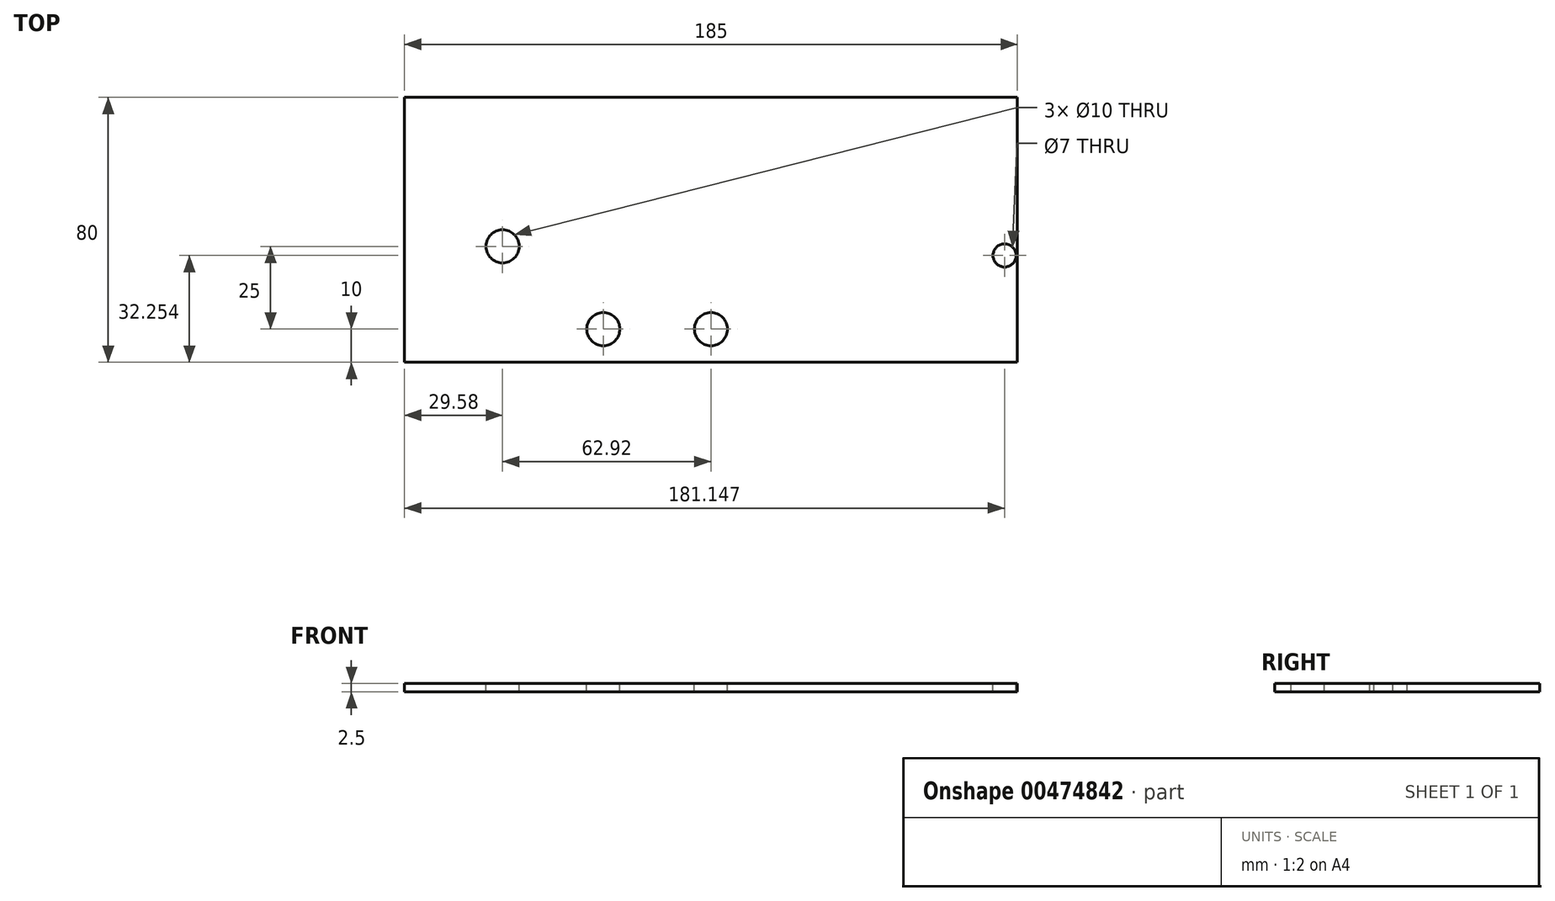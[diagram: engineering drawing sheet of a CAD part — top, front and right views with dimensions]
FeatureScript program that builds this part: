
annotation { "Feature Type Name" : "Feature", "Feature Type Description" : "" }
export const myFeature = defineFeature(function(context is Context, id is Id, definition is map)
    precondition{}
    {
        {
            var Q0;
            Q0=qCreatedBy(makeId("Top.planeOp"),FACE);
            var sketch = newSketch(context, id + "F0", { "sketchPlane" : qUnion([Q0])});
            skLineSegment(sketch, "E0.bottom", {"start": v(92.5, 40) * mm, "end": v(-92.5, 40) * mm});
            skLineSegment(sketch, "E0.top", {"start": v(92.5, -40) * mm, "end": v(-92.5, -40) * mm});
            skLineSegment(sketch, "E0.left", {"start": v(92.5, 40) * mm, "end": v(92.5, -40) * mm});
            skLineSegment(sketch, "E0.right", {"start": v(-92.5, 40) * mm, "end": v(-92.5, -40) * mm});
            skPoint(sketch, "E0.middle", {"position": v(0, 0) * mm});
            skSolve(sketch);
        }
        {
            var Q0;
            Q0 = qSketchRegion(id + "F0", true);
            extrude(context, id + "F1", {"entities" : qUnion([Q0]), "depth" : 2.5 * mm});
        }
        {
            var Q0;
            Q0=makeQuery(id+"F1.opExtrude","CAP_FACE",FACE,{"disambiguationData":[OSD([sQuery(id+"F0.wireOp",EDGE,"E0.bottom"),sQuery(id+"F0.wireOp",EDGE,"E0.top"),sQuery(id+"F0.wireOp",EDGE,"E0.left"),sQuery(id+"F0.wireOp",EDGE,"E0.right")])],"isStart":false});
            var sketch = newSketch(context, id + "F2", { "sketchPlane" : qUnion([Q0])});
            skCircle(sketch, "E1", {"center": v(-32.5, -30) * mm, "radius": 5 * mm});
            skCircle(sketch, "E2", {"center": v(0, -30) * mm, "radius": 5 * mm});
            skCircle(sketch, "E3", {"center": v(-62.92, -5) * mm, "radius": 5 * mm});
            skSolve(sketch);
        }
        {
            var Q0;
            Q0 = qSketchRegion(id + "F2", true);
            extrude(context, id + "F3", {"entities" : qUnion([Q0]), "operationType" : NewBodyOperationType.REMOVE, "oppositeDirection" : true, "depth" : 25 * mm});
        }
        {
            var Q0;
            Q0=makeQuery(id+"F1.opExtrude","CAP_FACE",FACE,{"disambiguationData":[OSD([sQuery(id+"F0.wireOp",EDGE,"E0.bottom"),sQuery(id+"F0.wireOp",EDGE,"E0.top"),sQuery(id+"F0.wireOp",EDGE,"E0.left"),sQuery(id+"F0.wireOp",EDGE,"E0.right")])],"isStart":false});
            var sketch = newSketch(context, id + "F4", { "sketchPlane" : qUnion([Q0])});
            skCircle(sketch, "E4", {"center": v(88.65, -7.75) * mm, "radius": 3.5 * mm});
            skSolve(sketch);
        }
        {
            var Q0;
            Q0 = qSketchRegion(id + "F4", true);
            extrude(context, id + "F5", {"entities" : qUnion([Q0]), "operationType" : NewBodyOperationType.REMOVE, "oppositeDirection" : true, "depth" : 25 * mm});
        }
    });
